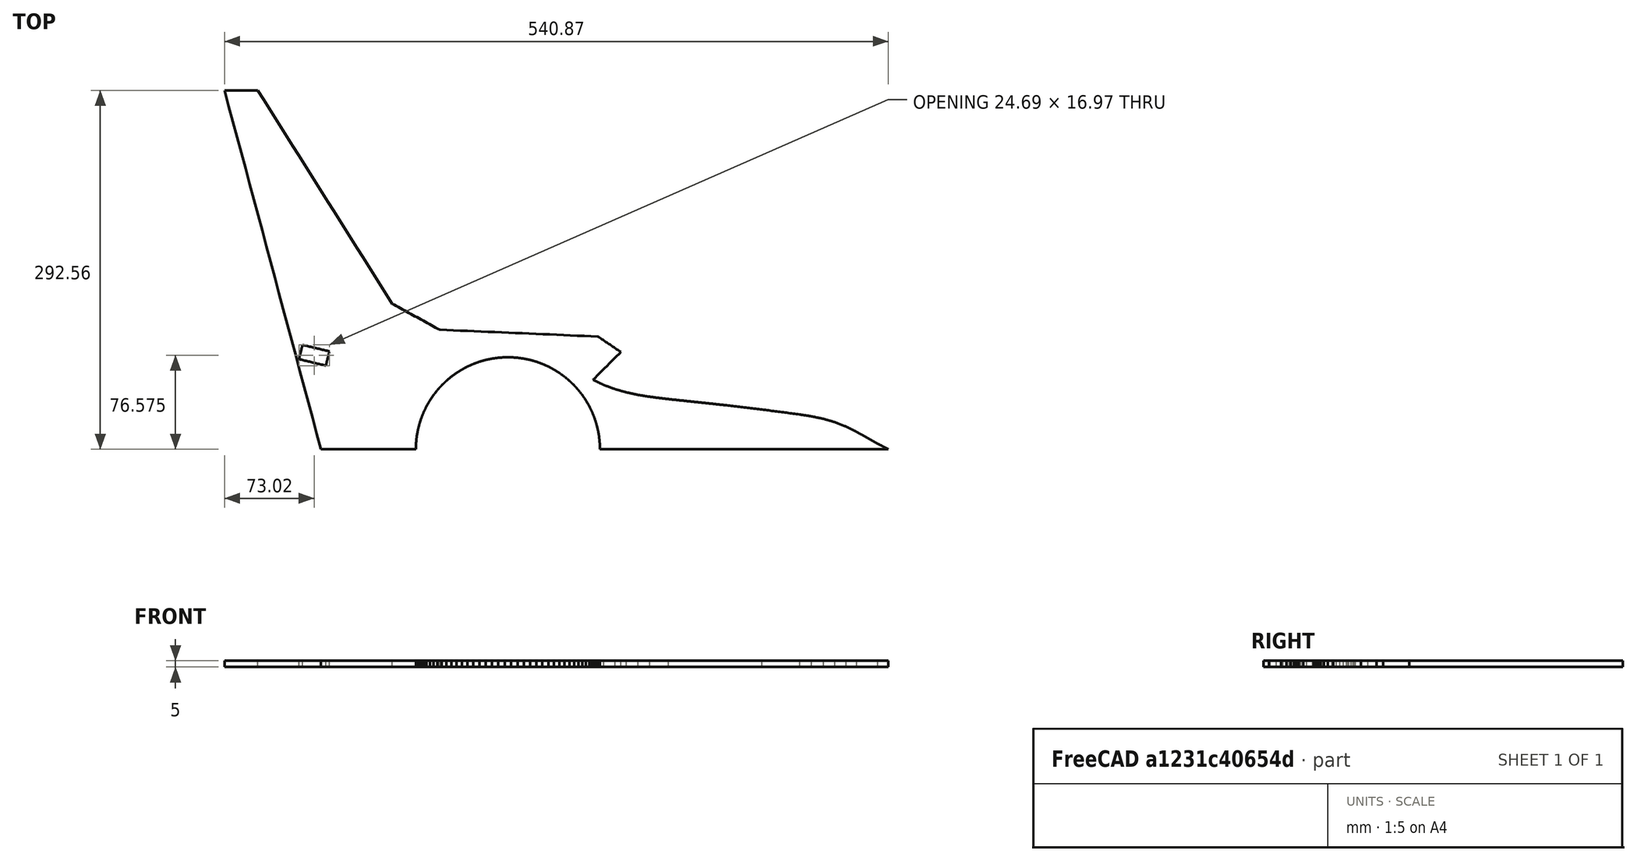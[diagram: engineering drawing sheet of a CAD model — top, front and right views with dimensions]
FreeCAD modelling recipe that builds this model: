
FCSTD DOCUMENT  (FreeCAD 0.19R)
Label: F-35_v2_parts_15
License: All rights reserved
LicenseURL: http://en.wikipedia.org/wiki/All_rights_reserved
objects: App::DocumentObjectGroup×2, PartDesign::CoordinateSystem×2, App::FeaturePython×1, Sketcher::SketchObject×1, PartDesign::Pad×1, PartDesign::Body×1, App::Part×1
note: 6 computed .brp shape members not serialized (recipe doc carries the construction recipe); baked Part::Feature solids carry a one-line shape summary decoded from their .brp

FEATURE [App::DocumentObjectGroup] Parts
FEATURE [PartDesign::CoordinateSystem] LCS_Origin
  AttacherType = Attacher::AttachEngine3D
  MapMode = 2
  Support = -> [X_Axis]
FEATURE [App::DocumentObjectGroup] Constraints
FEATURE [App::FeaturePython] Variables  # WARN: FeaturePython — macro-defined, semantics opaque (R4)
FEATURE [Sketcher::SketchObject] Sketch002
  FullyConstrained = false
  sketch-geometry (77):
    g0: BSplineCurve PolesCount=2 KnotsCount=2 Degree=1 IsPeriodic=0
    g1: BSplineCurve PolesCount=2 KnotsCount=2 Degree=1 IsPeriodic=0
    g2: BSplineCurve PolesCount=2 KnotsCount=2 Degree=1 IsPeriodic=0
    g3: BSplineCurve PolesCount=2 KnotsCount=2 Degree=1 IsPeriodic=0
    g4: BSplineCurve PolesCount=2 KnotsCount=2 Degree=1 IsPeriodic=0
    g5: BSplineCurve PolesCount=2 KnotsCount=2 Degree=1 IsPeriodic=0
    g6: BSplineCurve PolesCount=2 KnotsCount=2 Degree=1 IsPeriodic=0
    g7: BSplineCurve PolesCount=2 KnotsCount=2 Degree=1 IsPeriodic=0
    g8: BSplineCurve PolesCount=2 KnotsCount=2 Degree=1 IsPeriodic=0
    g9: BSplineCurve PolesCount=2 KnotsCount=2 Degree=1 IsPeriodic=0
    g10: BSplineCurve PolesCount=2 KnotsCount=2 Degree=1 IsPeriodic=0
    g11: BSplineCurve PolesCount=2 KnotsCount=2 Degree=1 IsPeriodic=0
    g12: BSplineCurve PolesCount=2 KnotsCount=2 Degree=1 IsPeriodic=0
    g13: BSplineCurve PolesCount=2 KnotsCount=2 Degree=1 IsPeriodic=0
    g14: BSplineCurve PolesCount=2 KnotsCount=2 Degree=1 IsPeriodic=0
    g15: BSplineCurve PolesCount=2 KnotsCount=2 Degree=1 IsPeriodic=0
    g16: BSplineCurve PolesCount=2 KnotsCount=2 Degree=1 IsPeriodic=0
    g17: BSplineCurve PolesCount=2 KnotsCount=2 Degree=1 IsPeriodic=0
    g18: BSplineCurve PolesCount=2 KnotsCount=2 Degree=1 IsPeriodic=0
    g19: BSplineCurve PolesCount=2 KnotsCount=2 Degree=1 IsPeriodic=0
    g20: BSplineCurve PolesCount=2 KnotsCount=2 Degree=1 IsPeriodic=0
    g21: BSplineCurve PolesCount=2 KnotsCount=2 Degree=1 IsPeriodic=0
    g22: BSplineCurve PolesCount=2 KnotsCount=2 Degree=1 IsPeriodic=0
    g23: BSplineCurve PolesCount=2 KnotsCount=2 Degree=1 IsPeriodic=0
    g24: BSplineCurve PolesCount=2 KnotsCount=2 Degree=1 IsPeriodic=0
    g25: BSplineCurve PolesCount=2 KnotsCount=2 Degree=1 IsPeriodic=0
    g26: BSplineCurve PolesCount=2 KnotsCount=2 Degree=1 IsPeriodic=0
    g27: BSplineCurve PolesCount=2 KnotsCount=2 Degree=1 IsPeriodic=0
    g28: BSplineCurve PolesCount=2 KnotsCount=2 Degree=1 IsPeriodic=0
    g29: BSplineCurve PolesCount=2 KnotsCount=2 Degree=1 IsPeriodic=0
    g30: BSplineCurve PolesCount=2 KnotsCount=2 Degree=1 IsPeriodic=0
    g31: BSplineCurve PolesCount=2 KnotsCount=2 Degree=1 IsPeriodic=0
    g32: BSplineCurve PolesCount=2 KnotsCount=2 Degree=1 IsPeriodic=0
    g33: BSplineCurve PolesCount=2 KnotsCount=2 Degree=1 IsPeriodic=0
    g34: BSplineCurve PolesCount=2 KnotsCount=2 Degree=1 IsPeriodic=0
    g35: BSplineCurve PolesCount=2 KnotsCount=2 Degree=1 IsPeriodic=0
    g36: BSplineCurve PolesCount=2 KnotsCount=2 Degree=1 IsPeriodic=0
    g37: BSplineCurve PolesCount=2 KnotsCount=2 Degree=1 IsPeriodic=0
    g38: BSplineCurve PolesCount=2 KnotsCount=2 Degree=1 IsPeriodic=0
    g39: BSplineCurve PolesCount=2 KnotsCount=2 Degree=1 IsPeriodic=0
    g40: BSplineCurve PolesCount=2 KnotsCount=2 Degree=1 IsPeriodic=0
    g41: BSplineCurve PolesCount=2 KnotsCount=2 Degree=1 IsPeriodic=0
    g42: BSplineCurve PolesCount=2 KnotsCount=2 Degree=1 IsPeriodic=0
    g43: BSplineCurve PolesCount=2 KnotsCount=2 Degree=1 IsPeriodic=0
    g44: BSplineCurve PolesCount=2 KnotsCount=2 Degree=1 IsPeriodic=0
    g45: BSplineCurve PolesCount=2 KnotsCount=2 Degree=1 IsPeriodic=0
    g46: BSplineCurve PolesCount=2 KnotsCount=2 Degree=1 IsPeriodic=0
    g47: BSplineCurve PolesCount=2 KnotsCount=2 Degree=1 IsPeriodic=0
    g48: BSplineCurve PolesCount=2 KnotsCount=2 Degree=1 IsPeriodic=0
    g49: BSplineCurve PolesCount=2 KnotsCount=2 Degree=1 IsPeriodic=0
    g50: BSplineCurve PolesCount=2 KnotsCount=2 Degree=1 IsPeriodic=0
    g51: BSplineCurve PolesCount=2 KnotsCount=2 Degree=1 IsPeriodic=0
    g52: BSplineCurve PolesCount=2 KnotsCount=2 Degree=1 IsPeriodic=0
    g53: BSplineCurve PolesCount=2 KnotsCount=2 Degree=1 IsPeriodic=0
    g54: BSplineCurve PolesCount=2 KnotsCount=2 Degree=1 IsPeriodic=0
    g55: BSplineCurve PolesCount=2 KnotsCount=2 Degree=1 IsPeriodic=0
    g56: BSplineCurve PolesCount=2 KnotsCount=2 Degree=1 IsPeriodic=0
    g57: BSplineCurve PolesCount=2 KnotsCount=2 Degree=1 IsPeriodic=0
    g58: BSplineCurve PolesCount=2 KnotsCount=2 Degree=1 IsPeriodic=0
    g59: BSplineCurve PolesCount=2 KnotsCount=2 Degree=1 IsPeriodic=0
    g60: BSplineCurve PolesCount=2 KnotsCount=2 Degree=1 IsPeriodic=0
    g61: BSplineCurve PolesCount=2 KnotsCount=2 Degree=1 IsPeriodic=0
    g62: BSplineCurve PolesCount=2 KnotsCount=2 Degree=1 IsPeriodic=0
    g63: BSplineCurve PolesCount=2 KnotsCount=2 Degree=1 IsPeriodic=0
    g64: BSplineCurve PolesCount=2 KnotsCount=2 Degree=1 IsPeriodic=0
    g65: BSplineCurve PolesCount=2 KnotsCount=2 Degree=1 IsPeriodic=0
    g66: BSplineCurve PolesCount=2 KnotsCount=2 Degree=1 IsPeriodic=0
    g67: BSplineCurve PolesCount=2 KnotsCount=2 Degree=1 IsPeriodic=0
    g68: BSplineCurve PolesCount=2 KnotsCount=2 Degree=1 IsPeriodic=0
    g69: BSplineCurve PolesCount=2 KnotsCount=2 Degree=1 IsPeriodic=0
    g70: BSplineCurve PolesCount=2 KnotsCount=2 Degree=1 IsPeriodic=0
    g71: BSplineCurve PolesCount=2 KnotsCount=2 Degree=1 IsPeriodic=0
    g72: BSplineCurve PolesCount=2 KnotsCount=2 Degree=1 IsPeriodic=0
    g73: BSplineCurve PolesCount=2 KnotsCount=2 Degree=1 IsPeriodic=0
    g74: BSplineCurve PolesCount=2 KnotsCount=2 Degree=1 IsPeriodic=0
    g75: BSplineCurve PolesCount=2 KnotsCount=2 Degree=1 IsPeriodic=0
    g76: BSplineCurve PolesCount=2 KnotsCount=2 Degree=1 IsPeriodic=0
  constraints (62):
    c: Coincident(g6,g7)
    c: Coincident(g7,g8)
    c: Coincident(g8,g9)
    c: Coincident(g9,g10)
    c: Coincident(g10,g11)
    c: Coincident(g11,g12)
    c: Coincident(g12,g13)
    c: Coincident(g13,g14)
    c: Coincident(g14,g15)
    c: Coincident(g15,g16)
    c: Coincident(g16,g17)
    c: Coincident(g17,g18)
    c: Coincident(g18,g19)
    c: Coincident(g19,g20)
    c: Coincident(g20,g21)
    c: Coincident(g21,g22)
    c: Coincident(g22,g23)
    c: Coincident(g23,g24)
    c: Coincident(g25,g26)
    c: Coincident(g26,g27)
    c: Coincident(g27,g28)
    c: Coincident(g28,g29)
    c: Coincident(g29,g30)
    c: Coincident(g30,g31)
    c: Coincident(g31,g32)
    c: Coincident(g32,g33)
    c: Coincident(g33,g34)
    c: Coincident(g34,g35)
    c: Coincident(g35,g36)
    c: Coincident(g36,g37)
    c: Coincident(g37,g38)
    c: Coincident(g38,g39)
    c: Coincident(g39,g40)
    c: Coincident(g40,g41)
    c: Coincident(g41,g42)
    c: Coincident(g42,g43)
    c: Coincident(g43,g44)
    c: Coincident(g44,g45)
    c: Coincident(g45,g46)
    c: Coincident(g46,g47)
    c: Coincident(g47,g48)
    c: Coincident(g48,g49)
    c: Coincident(g49,g50)
    c: Coincident(g50,g51)
    c: Coincident(g51,g52)
    c: Coincident(g52,g53)
    c: Coincident(g53,g54)
    c: Coincident(g54,g55)
    c: Coincident(g55,g56)
    c: Coincident(g56,g57)
    c: Coincident(g57,g58)
    c: Coincident(g58,g59)
    c: Coincident(g59,g60)
    c: Coincident(g60,g61)
    c: Coincident(g61,g62)
    c: Coincident(g62,g63)
    c: Coincident(g63,g64)
    c: Coincident(g64,g65)
    c: Coincident(g65,g66)
    c: Coincident(g66,g67)
    c: Coincident(g67,g68)
    c: Coincident(g68,g69)
FEATURE [PartDesign::Pad] Pad004
  Direction = (1,1,1)
  Length = 5
  Length2 = 100
  Profile = -> Sketch002
  Type = 0
FEATURE [PartDesign::Body] Body002  label="Part15"
  Group = -> [Sketch002,Pad004]
  Origin = -> Origin003
  Tip = -> Pad004
FEATURE [PartDesign::CoordinateSystem] LCS_1
  AttacherType = Attacher::AttachEngine3D
  MapMode = 7
  Placement = pos=(412.949,-397.985,0) rot=(0,1,0;3.14159rad)
  Support = -> [Pad004]
FEATURE [App::Part] Model
  Configuration = 0
  Group = -> [LCS_Origin,Constraints,Variables,Body002,LCS_1]
  Origin = -> Origin
  Type = Assembly4 Model
